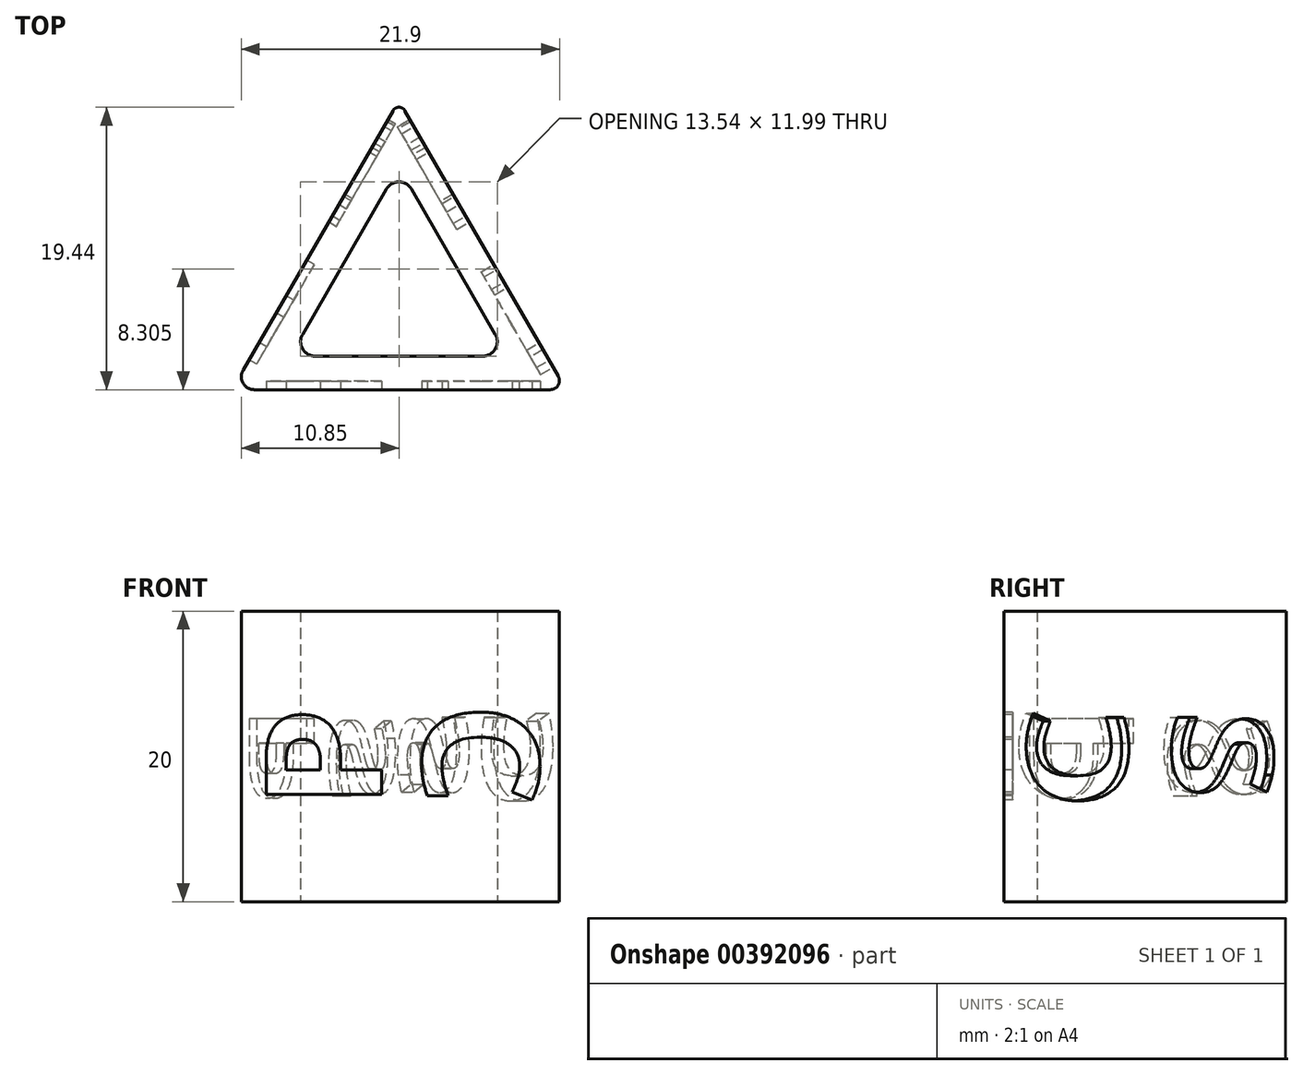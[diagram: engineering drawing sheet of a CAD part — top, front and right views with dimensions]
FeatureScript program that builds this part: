
annotation { "Feature Type Name" : "Feature", "Feature Type Description" : "" }
export const myFeature = defineFeature(function(context is Context, id is Id, definition is map)
    precondition{}
    {
        {
            var Q0;
            Q0=qCreatedBy(makeId("Top.planeOp"),FACE);
            var sketch = newSketch(context, id + "F0", { "sketchPlane" : qUnion([Q0])});
            skCircle(sketch, "E0.cCircle", {"center": v(0, 0) * mm, "radius": 6.64 * mm, "construction": true});
            skLineSegment(sketch, "E0.0", {"start": v(10.42, -6.64) * mm, "end": v(-9.96, -6.64) * mm});
            skLineSegment(sketch, "E0.1", {"start": v(-10.73, -5.3) * mm, "end": v(-0.41, 12.57) * mm});
            skLineSegment(sketch, "E0.2", {"start": v(0.41, 12.57) * mm, "end": v(10.96, -5.7) * mm});
            skPoint(sketch, "E0.0.midPoint", {"position": v(0, -6.64) * mm});
            skCircle(sketch, "E1.cCircle", {"center": v(0, 0) * mm, "radius": 4.33 * mm, "construction": true});
            skLineSegment(sketch, "E1.0", {"start": v(5.77, -4.33) * mm, "end": v(-5.77, -4.33) * mm});
            skLineSegment(sketch, "E1.1", {"start": v(-6.63, -2.83) * mm, "end": v(-0.87, 7.16) * mm});
            skLineSegment(sketch, "E1.2", {"start": v(0.87, 7.16) * mm, "end": v(6.63, -2.83) * mm});
            skPoint(sketch, "E1.0.midPoint", {"position": v(0, -4.33) * mm});
            skPoint(sketch, "E2.visualSharp", {"position": v(0, 8.66) * mm});
            skPoint(sketch, "E3.visualSharp", {"position": v(0, 13.28) * mm});
            skArc(sketch, "E3.filletArc", {"start": v(0.41, 12.57) * mm, "mid": v(0, 12.8) * mm, "end": v(-0.41, 12.57) * mm});
            skPoint(sketch, "E4.visualSharp", {"position": v(7.5, -4.33) * mm});
            skPoint(sketch, "E5.visualSharp", {"position": v(11.5, -6.64) * mm});
            skArc(sketch, "E5.filletArc", {"start": v(10.42, -6.64) * mm, "mid": v(10.96, -6.33) * mm, "end": v(10.96, -5.7) * mm});
            skPoint(sketch, "E6.visualSharp", {"position": v(-7.5, -4.33) * mm});
            skPoint(sketch, "E7.visualSharp", {"position": v(-11.5, -6.64) * mm});
            skArc(sketch, "E7.filletArc", {"start": v(-10.73, -5.3) * mm, "mid": v(-10.73, -6.2) * mm, "end": v(-9.96, -6.64) * mm});
            skArc(sketch, "E8.filletArc", {"start": v(0.87, 7.16) * mm, "mid": v(0, 7.66) * mm, "end": v(-0.87, 7.16) * mm});
            skArc(sketch, "E9.filletArc", {"start": v(5.77, -4.33) * mm, "mid": v(6.63, -3.83) * mm, "end": v(6.63, -2.83) * mm});
            skArc(sketch, "E10.filletArc", {"start": v(-6.63, -2.83) * mm, "mid": v(-6.63, -3.83) * mm, "end": v(-5.77, -4.33) * mm});
            skSolve(sketch);
        }
        {
            var Q0;
            Q0=makeQuery(id+"F0.imprint","IMPRINT",FACE,{"disambiguationData":[TD([[makeQuery(id+"F0.imprint","IMPRINT",EDGE,{"derivedFrom":sQuery(id+"F0.wireOp",EDGE,"E0.0")}),-1.0]])]});
            extrude(context, id + "F1", {"entities" : qUnion([Q0]), "depth" : 20 * mm});
        }
        {
            var Q0;
            Q0=makeQuery(id+"F1.opExtrude","SWEPT_FACE",FACE,{"disambiguationData":[OSD([sQuery(id+"F0.wireOp",EDGE,"E0.2")])]});
            var sketch = newSketch(context, id + "F2", { "sketchPlane" : qUnion([Q0])});
            skText(sketch, "E11", { "text": "S", "fontName": "OpenSans-Bold.ttf"});
            skText(sketch, "E12", { "text": "C", "fontName": "OpenSans-Bold.ttf"});
            const initialGuessF2  = {"E11": [0.00193, 0.0132, 0, -1, 0.008], "E12": [-0.00167, 0.0063, 0, 1, 0.008]};
            skSetInitialGuess(sketch, initialGuessF2);
            skSolve(sketch);
        }
        {
            var Q0;
            Q0=makeQuery(id+"F1.opExtrude","SWEPT_FACE",FACE,{"disambiguationData":[OSD([sQuery(id+"F0.wireOp",EDGE,"E0.1")])]});
            var sketch = newSketch(context, id + "F3", { "sketchPlane" : qUnion([Q0])});
            skText(sketch, "E13", { "text": "S", "fontName": "OpenSans-Bold.ttf"});
            skText(sketch, "E14", { "text": "P", "fontName": "OpenSans-Bold.ttf"});
            const initialGuessF3  = {"E13": [-0.00193, 0.0068, 0, 1, 0.008], "E14": [0.0012, 0.0136, 0, -1, 0.008]};
            skSetInitialGuess(sketch, initialGuessF3);
            skSolve(sketch);
        }
        {
            var Q0;
            Q0=makeQuery(id+"F1.opExtrude","SWEPT_FACE",FACE,{"disambiguationData":[OSD([sQuery(id+"F0.wireOp",EDGE,"E0.0")])]});
            var sketch = newSketch(context, id + "F4", { "sketchPlane" : qUnion([Q0])});
            skText(sketch, "E15", { "text": "P", "fontName": "OpenSans-Bold.ttf"});
            skText(sketch, "E16", { "text": "C", "fontName": "OpenSans-Bold.ttf"});
            const initialGuessF4  = {"E15": [-0.0012, 0.0064, 0, 1, 0.008], "E16": [0.00167, 0.0137, 0, -1, 0.008]};
            skSetInitialGuess(sketch, initialGuessF4);
            skSolve(sketch);
        }
        {
            var Q0;
            Q0=makeQuery(id+"F2.imprint","IMPRINT",FACE,{"disambiguationData":[TD([[makeQuery(id+"F2.imprint","IMPRINT",EDGE,{"derivedFrom":sQuery(id+"F2.wireOp",EDGE,"E12.sketch_text.stroke-0")}),-1.0]])]});
            var Q1;
            Q1=makeQuery(id+"F2.imprint","IMPRINT",FACE,{"disambiguationData":[TD([[makeQuery(id+"F2.imprint","IMPRINT",EDGE,{"derivedFrom":sQuery(id+"F2.wireOp",EDGE,"E11.sketch_text.stroke-0")}),-1.0]])]});
            extrude(context, id + "F5", {"entities" : qUnion([Q0, Q1]), "operationType" : NewBodyOperationType.REMOVE, "oppositeDirection" : true, "depth" : 1 * mm});
        }
        {
            var Q0;
            Q0=makeQuery(id+"F3.imprint","IMPRINT",FACE,{"disambiguationData":[TD([[makeQuery(id+"F3.imprint","IMPRINT",EDGE,{"derivedFrom":sQuery(id+"F3.wireOp",EDGE,"E13.sketch_text.stroke-0")}),-1.0]])]});
            var Q1;
            Q1=makeQuery(id+"F3.imprint","IMPRINT",FACE,{"disambiguationData":[TD([[makeQuery(id+"F3.imprint","IMPRINT",EDGE,{"derivedFrom":sQuery(id+"F3.wireOp",EDGE,"E14.sketch_text.stroke-0")}),-1.0]])]});
            extrude(context, id + "F6", {"entities" : qUnion([Q0, Q1]), "operationType" : NewBodyOperationType.REMOVE, "oppositeDirection" : true, "depth" : 0.6 * mm});
        }
        {
            var Q0;
            Q0=makeQuery(id+"F4.imprint","IMPRINT",FACE,{"disambiguationData":[TD([[makeQuery(id+"F4.imprint","IMPRINT",EDGE,{"derivedFrom":sQuery(id+"F4.wireOp",EDGE,"E15.sketch_text.stroke-0")}),-1.0]])]});
            var Q1;
            Q1=makeQuery(id+"F4.imprint","IMPRINT",FACE,{"disambiguationData":[TD([[makeQuery(id+"F4.imprint","IMPRINT",EDGE,{"derivedFrom":sQuery(id+"F4.wireOp",EDGE,"E16.sketch_text.stroke-0")}),-1.0]])]});
            extrude(context, id + "F7", {"entities" : qUnion([Q0, Q1]), "operationType" : NewBodyOperationType.REMOVE, "oppositeDirection" : true, "depth" : 0.6 * mm});
        }
    });
